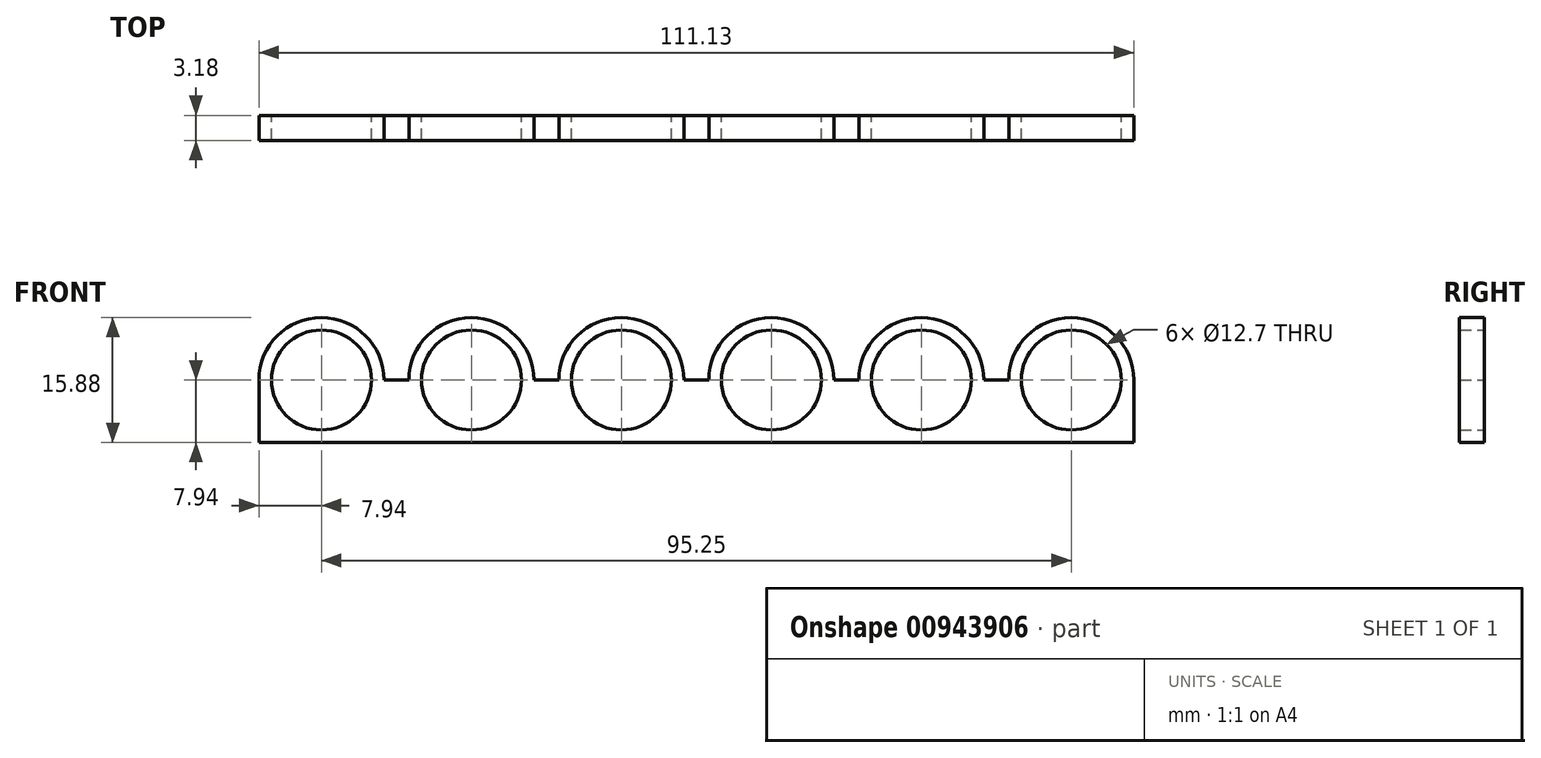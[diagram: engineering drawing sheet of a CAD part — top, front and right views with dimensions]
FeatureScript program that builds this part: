
annotation { "Feature Type Name" : "Feature", "Feature Type Description" : "" }
export const myFeature = defineFeature(function(context is Context, id is Id, definition is map)
    precondition{}
    {
        {
            var Q0;
            Q0=qCreatedBy(makeId("Front.planeOp"),FACE);
            var sketch = newSketch(context, id + "F0", { "sketchPlane" : qUnion([Q0])});
            skLineSegment(sketch, "E0", {"start": v(0, 0) * mm, "end": v(-6.35, 0) * mm});
            skLineSegment(sketch, "E1", {"start": v(-6.35, 0) * mm, "end": v(-7.94, 0) * mm});
            skLineSegment(sketch, "E2", {"start": v(-7.94, 0) * mm, "end": v(-11.11, 0) * mm});
            skLineSegment(sketch, "E3", {"start": v(-11.11, 0) * mm, "end": v(-12.7, 0) * mm});
            skLineSegment(sketch, "E4", {"start": v(-12.7, 0) * mm, "end": v(-19.05, 0) * mm});
            skLineSegment(sketch, "E5", {"start": v(-19.05, 0) * mm, "end": v(-25.4, 0) * mm});
            skLineSegment(sketch, "E6", {"start": v(-25.4, 0) * mm, "end": v(-26.99, 0) * mm});
            skLineSegment(sketch, "E7", {"start": v(-26.99, 0) * mm, "end": v(-30.16, 0) * mm});
            skLineSegment(sketch, "E8", {"start": v(-30.16, 0) * mm, "end": v(-31.75, 0) * mm});
            skLineSegment(sketch, "E9", {"start": v(-31.75, 0) * mm, "end": v(-38.1, 0) * mm});
            skLineSegment(sketch, "E10", {"start": v(-38.1, 0) * mm, "end": v(-44.45, 0) * mm});
            skLineSegment(sketch, "E11", {"start": v(-44.45, 0) * mm, "end": v(-46.04, 0) * mm});
            skLineSegment(sketch, "E12", {"start": v(-46.04, 0) * mm, "end": v(-49.21, 0) * mm});
            skLineSegment(sketch, "E13", {"start": v(-49.21, 0) * mm, "end": v(-50.8, 0) * mm});
            skLineSegment(sketch, "E14", {"start": v(-50.8, 0) * mm, "end": v(-57.15, 0) * mm});
            skLineSegment(sketch, "E15", {"start": v(-57.15, 0) * mm, "end": v(-63.5, 0) * mm});
            skLineSegment(sketch, "E16", {"start": v(-63.5, 0) * mm, "end": v(-65.09, 0) * mm});
            skLineSegment(sketch, "E17", {"start": v(-65.09, 0) * mm, "end": v(-68.26, 0) * mm});
            skLineSegment(sketch, "E18", {"start": v(-68.26, 0) * mm, "end": v(-69.85, 0) * mm});
            skLineSegment(sketch, "E19", {"start": v(-69.85, 0) * mm, "end": v(-76.2, 0) * mm});
            skLineSegment(sketch, "E20", {"start": v(-76.2, 0) * mm, "end": v(-82.55, 0) * mm});
            skLineSegment(sketch, "E21", {"start": v(-82.55, 0) * mm, "end": v(-84.14, 0) * mm});
            skCircle(sketch, "E22", {"center": v(0, 0) * mm, "radius": 6.35 * mm});
            skCircle(sketch, "E23", {"center": v(0, 0) * mm, "radius": 7.94 * mm});
            skCircle(sketch, "E24", {"center": v(-19.05, 0) * mm, "radius": 6.35 * mm});
            skCircle(sketch, "E25", {"center": v(-19.05, 0) * mm, "radius": 7.94 * mm});
            skCircle(sketch, "E26", {"center": v(-38.1, 0) * mm, "radius": 6.35 * mm});
            skCircle(sketch, "E27", {"center": v(-38.1, 0) * mm, "radius": 7.94 * mm});
            skCircle(sketch, "E28", {"center": v(-57.15, 0) * mm, "radius": 6.35 * mm});
            skCircle(sketch, "E29", {"center": v(-57.15, 0) * mm, "radius": 7.94 * mm});
            skCircle(sketch, "E30", {"center": v(-76.2, 0) * mm, "radius": 6.35 * mm});
            skCircle(sketch, "E31", {"center": v(-76.2, 0) * mm, "radius": 7.94 * mm});
            skLineSegment(sketch, "E32", {"start": v(-84.14, 0) * mm, "end": v(-87.31, 0) * mm});
            skLineSegment(sketch, "E33", {"start": v(-87.31, 0) * mm, "end": v(-88.9, 0) * mm});
            skLineSegment(sketch, "E34", {"start": v(-88.9, 0) * mm, "end": v(-95.25, 0) * mm});
            skCircle(sketch, "E35", {"center": v(-95.25, 0) * mm, "radius": 7.94 * mm});
            skCircle(sketch, "E36", {"center": v(-95.25, 0) * mm, "radius": 6.35 * mm});
            skLineSegment(sketch, "E37", {"start": v(-95.25, 0) * mm, "end": v(-103.19, 0) * mm});
            skLineSegment(sketch, "E38", {"start": v(0, 0) * mm, "end": v(7.94, 0) * mm});
            skLineSegment(sketch, "E39", {"start": v(0, 0) * mm, "end": v(0, -7.94) * mm});
            skLineSegment(sketch, "E40", {"start": v(-95.25, 0) * mm, "end": v(-95.25, -7.94) * mm});
            skLineSegment(sketch, "E41", {"start": v(7.94, 0) * mm, "end": v(7.94, -7.94) * mm});
            skLineSegment(sketch, "E42", {"start": v(-103.19, 0) * mm, "end": v(-103.19, -7.94) * mm});
            skLineSegment(sketch, "E43", {"start": v(-103.19, -7.94) * mm, "end": v(7.94, -7.94) * mm});
            skLineSegment(sketch, "E44", {"start": v(7.94, -7.94) * mm, "end": v(7.94, -9.52) * mm});
            skLineSegment(sketch, "E45", {"start": v(7.94, -9.52) * mm, "end": v(-103.19, -9.52) * mm});
            skLineSegment(sketch, "E46", {"start": v(-103.19, -9.52) * mm, "end": v(-103.19, -7.94) * mm});
            skSolve(sketch);
        }
        {
            var Q0;
            Q0 = qSketchRegion(id + "F0", true);
            extrude(context, id + "F1", {"entities" : qUnion([Q0]), "depth" : 3.17 * mm, "offsetDistance" : 25.4 * mm});
        }
        {
            var Q0;
            Q0=makeQuery(id+"F1.opExtrude","CAP_FACE",FACE,{"disambiguationData":[OSD([sQuery(id+"F0.wireOp",EDGE,"E2"),sQuery(id+"F0.wireOp",EDGE,"E7"),sQuery(id+"F0.wireOp",EDGE,"E12"),sQuery(id+"F0.wireOp",EDGE,"E17"),sQuery(id+"F0.wireOp",EDGE,"E22"),sQuery(id+"F0.wireOp",EDGE,"E23"),sQuery(id+"F0.wireOp",EDGE,"E24"),sQuery(id+"F0.wireOp",EDGE,"E25"),sQuery(id+"F0.wireOp",EDGE,"E26"),sQuery(id+"F0.wireOp",EDGE,"E27"),sQuery(id+"F0.wireOp",EDGE,"E28"),sQuery(id+"F0.wireOp",EDGE,"E29"),sQuery(id+"F0.wireOp",EDGE,"E30"),sQuery(id+"F0.wireOp",EDGE,"E31"),sQuery(id+"F0.wireOp",EDGE,"E32"),sQuery(id+"F0.wireOp",EDGE,"E35"),sQuery(id+"F0.wireOp",EDGE,"E36"),sQuery(id+"F0.wireOp",EDGE,"E41"),sQuery(id+"F0.wireOp",EDGE,"E42"),sQuery(id+"F0.wireOp",EDGE,"E44"),sQuery(id+"F0.wireOp",EDGE,"E45"),sQuery(id+"F0.wireOp",EDGE,"E46")])],"isStart":false});
            var sketch = newSketch(context, id + "F2", { "sketchPlane" : qUnion([Q0])});
            skLineSegment(sketch, "E47", {"start": v(-103.19, -9.52) * mm, "end": v(-103.19, -7.94) * mm});
            skLineSegment(sketch, "E48", {"start": v(-103.19, -9.52) * mm, "end": v(7.94, -9.52) * mm});
            skLineSegment(sketch, "E49", {"start": v(7.94, -9.52) * mm, "end": v(7.94, -7.94) * mm});
            skLineSegment(sketch, "E50", {"start": v(7.94, -7.94) * mm, "end": v(-103.19, -7.94) * mm});
            skSolve(sketch);
        }
        {
            var Q0;
            Q0 = qSketchRegion(id + "F2", true);
            extrude(context, id + "F3", {"entities" : qUnion([Q0]), "operationType" : NewBodyOperationType.ADD, "depth" : 15.88 * mm, "offsetDistance" : 25.4 * mm});
        }
        {
            var Q0;
            Q0=makeQuery(id+"F3.boolean.opBoolean","MERGE",FACE,{"derivedFrom":[makeQuery(id+"F1.opExtrude","SWEPT_FACE",FACE,{"disambiguationData":[OSD([sQuery(id+"F0.wireOp",EDGE,"E45")])]}),makeQuery(id+"F3.opExtrude","SWEPT_FACE",FACE,{"disambiguationData":[OSD([sQuery(id+"F2.wireOp",EDGE,"E48")])]})]});
            var sketch = newSketch(context, id + "F4", { "sketchPlane" : qUnion([Q0])});
            skLineSegment(sketch, "E51.bottom", {"start": v(-103.19, 0) * mm, "end": v(7.94, 0) * mm});
            skLineSegment(sketch, "E51.top", {"start": v(-103.19, 19.05) * mm, "end": v(7.94, 19.05) * mm});
            skLineSegment(sketch, "E51.left", {"start": v(-103.19, 0) * mm, "end": v(-103.19, 19.05) * mm});
            skLineSegment(sketch, "E51.right", {"start": v(7.94, 0) * mm, "end": v(7.94, 19.05) * mm});
            skSolve(sketch);
        }
        {
            var Q0;
            Q0 = qSketchRegion(id + "F4", true);
            extrude(context, id + "F5", {"entities" : qUnion([Q0]), "operationType" : NewBodyOperationType.ADD, "depth" : 1.57 * mm, "offsetDistance" : 25.4 * mm});
        }
        {
            var Q0;
            Q0=makeQuery(id+"F5.boolean.opBoolean","MERGE",FACE,{"derivedFrom":[makeQuery(id+"F3.opExtrude","CAP_FACE",FACE,{"disambiguationData":[OSD([sQuery(id+"F2.wireOp",EDGE,"E47"),sQuery(id+"F2.wireOp",EDGE,"E48"),sQuery(id+"F2.wireOp",EDGE,"E49"),sQuery(id+"F2.wireOp",EDGE,"E50")])],"isStart":false}),makeQuery(id+"F5.opExtrude","SWEPT_FACE",FACE,{"disambiguationData":[OSD([sQuery(id+"F4.wireOp",EDGE,"E51.top")])]})]});
            var sketch = newSketch(context, id + "F6", { "sketchPlane" : qUnion([Q0])});
            skLineSegment(sketch, "E52", {"start": v(-103.19, -11.1) * mm, "end": v(-103.19, -7.94) * mm});
            skLineSegment(sketch, "E53", {"start": v(-103.19, -7.94) * mm, "end": v(7.94, -7.94) * mm});
            skLineSegment(sketch, "E54", {"start": v(7.94, -7.94) * mm, "end": v(7.94, -11.1) * mm});
            skLineSegment(sketch, "E55", {"start": v(7.94, -11.1) * mm, "end": v(-103.19, -11.1) * mm});
            skSolve(sketch);
        }
        {
            var Q0;
            Q0 = qSketchRegion(id + "F6", true);
            extrude(context, id + "F7", {"entities" : qUnion([Q0]), "operationType" : NewBodyOperationType.REMOVE, "oppositeDirection" : true, "depth" : 25.4 * mm, "offsetDistance" : 25.4 * mm});
        }
    });
